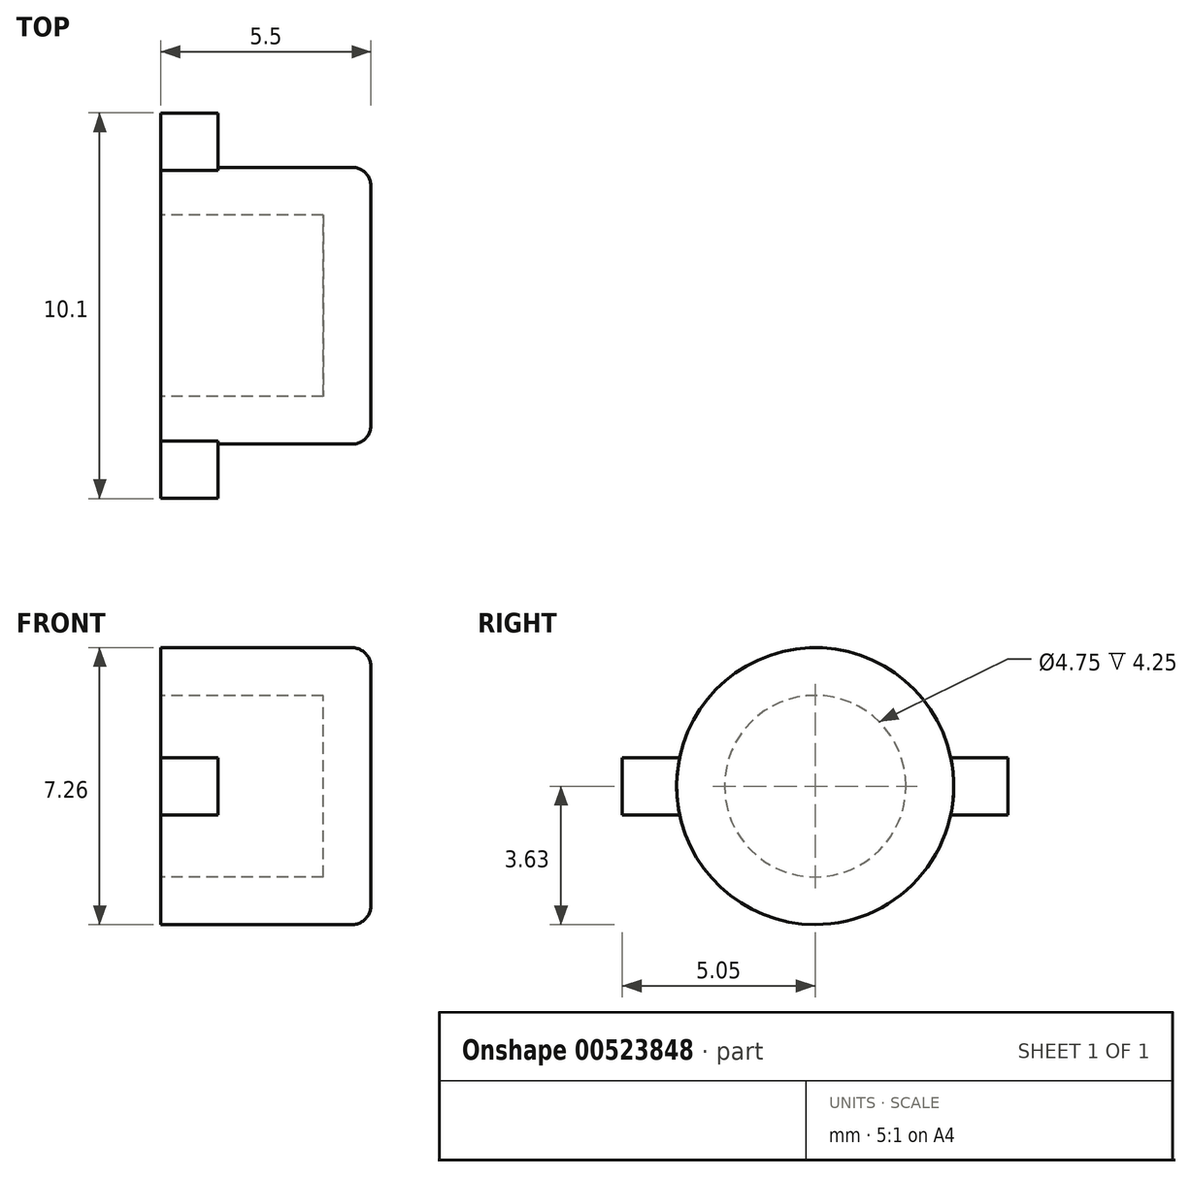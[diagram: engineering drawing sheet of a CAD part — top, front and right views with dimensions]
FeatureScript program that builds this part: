
annotation { "Feature Type Name" : "Feature", "Feature Type Description" : "" }
export const myFeature = defineFeature(function(context is Context, id is Id, definition is map)
    precondition{}
    {
        {
            var Q0;
            Q0=qCreatedBy(makeId("Right.planeOp"),FACE);
            var sketch = newSketch(context, id + "F0", { "sketchPlane" : qUnion([Q0])});
            skCircle(sketch, "E0", {"center": v(0, 0) * mm, "radius": 3.62 * mm});
            skSolve(sketch);
        }
        {
            var Q0;
            Q0=makeQuery(id+"F0.imprint","IMPRINT",FACE,{"disambiguationData":[TD([[makeQuery(id+"F0.imprint","IMPRINT",EDGE,{"derivedFrom":sQuery(id+"F0.wireOp",EDGE,"E0")}),1.0]])]});
            extrude(context, id + "F1", {"entities" : qUnion([Q0]), "endBound" : BoundingType.SYMMETRIC, "depth" : 5.5 * mm, "offsetDistance" : 25 * mm});
        }
        {
            var Q0;
            Q0=makeQuery(id+"F1.opExtrude","CAP_FACE",FACE,{"disambiguationData":[OSD([sQuery(id+"F0.wireOp",EDGE,"E0")])],"isStart":false});
            fillet(context, id + "F2", {"entities" : qUnion([Q0]), "radius" : 0.5 * mm, "tangentPropagation" : true, "allowEdgeOverflow" : false});
        }
        {
            var Q0;
            Q0=makeQuery(id+"F1.opExtrude","CAP_FACE",FACE,{"disambiguationData":[OSD([sQuery(id+"F0.wireOp",EDGE,"E0")])],"isStart":true});
            shell(context, id + "F3", {"entities" : qUnion([Q0]), "thickness" : 1.25 * mm});
        }
        {
            var Q0;
            Q0=makeQuery(id+"F1.opExtrude","CAP_FACE",FACE,{"disambiguationData":[OSD([sQuery(id+"F0.wireOp",EDGE,"E0")])],"isStart":true});
            var sketch = newSketch(context, id + "F4", { "sketchPlane" : qUnion([Q0])});
            skLineSegment(sketch, "E1.left", {"start": v(5.05, -0.75) * mm, "end": v(5.05, 0.75) * mm});
            skLineSegment(sketch, "E2.left", {"start": v(-5.05, 0.75) * mm, "end": v(-5.05, -0.75) * mm});
            skLineSegment(sketch, "E3", {"start": v(5.05, 0.75) * mm, "end": v(3.55, 0.75) * mm});
            skLineSegment(sketch, "E4", {"start": v(5.05, -0.75) * mm, "end": v(3.55, -0.75) * mm});
            skArc(sketch, "E5", {"start": v(-3.55, 0.75) * mm, "mid": v(-3.63, 0) * mm, "end": v(-3.55, -0.75) * mm});
            skLineSegment(sketch, "E6", {"start": v(-5.05, 0.75) * mm, "end": v(-3.55, 0.75) * mm});
            skLineSegment(sketch, "E7", {"start": v(-5.05, -0.75) * mm, "end": v(-3.55, -0.75) * mm});
            skArc(sketch, "E8.trimOffspring", {"start": v(3.55, -0.75) * mm, "mid": v(3.63, 0) * mm, "end": v(3.55, 0.75) * mm});
            skPoint(sketch, "E9", {"position": v(5.05, 0) * mm});
            skPoint(sketch, "E10", {"position": v(-5.05, 0) * mm});
            skSolve(sketch);
        }
        {
            var Q0;
            Q0 = qSketchRegion(id + "F4", true);
            extrude(context, id + "F5", {"entities" : qUnion([Q0]), "operationType" : NewBodyOperationType.ADD, "oppositeDirection" : true, "depth" : 1.5 * mm, "offsetDistance" : 25 * mm});
        }
    });
